# Revit family: Planet-Wattohm Mini Colonnes Logix Clippage direct
name_source: partatom
category: Installations électriques
units: mm (PartAtom-declared; Revit-internal decimal feet)

## family parameters
Basée sur le plan de construction = Non
Conserver l'orientation des annotations = Non
Cote de connecteur circulaire = Utiliser le diamètre
Couper avec des vides une fois chargée = Non
Partagée = Non
Point de calcul de pièce = Non
Toujours verticalement = Oui
Type d'élément = Normal

## types (6) — shared parameters
Column stand = Pied mobile : pied pr Colonnette Alu 1/2 cpt
Fabricant = PLANET WATTOHM
Finition = Aluminium
Matériau couvercle = Legrand - Plastique gris
Matériaux corps = Legrand - Aluminium gris
Standard = A clippage direct-ON
zero-valued in all types: Elévation par défaut

## per-type parameters (varying)
| type | 1 CPT | 2 CPT | 4 CPT | Description | H1 | HC | Largeur | Longueur | Matériau principal | Modèle | Nombre de compartiments | Séparateur |
| Colonnette 1 cpt 0,30m Alu | Oui | Non | Non | Colonne mobile 1 compartiment, 2 faces. Clippage direct. Logix 45. Corps en et couvercles en Aluminium. 2m | 300 mm | 260 mm  [stored 0.853018 ft] | 75 mm  [stored 0.246063 ft] | 82 mm  [stored 0.269029 ft] | Aluminium | PW-32315 | 1 compartiment | 35 mm |
| Colonnette 1 cpt 0,68m Alu | Oui | Non | Non | Colonnette 1 compartiment. Clippage direct. Logix 45. En Aluminium. 0,30m | 680 mm  [stored 2.23097 ft] | 640 mm  [stored 2.09974 ft] | 75 mm  [stored 0.246063 ft] | 82 mm  [stored 0.269029 ft] | Aluminium | PW-32316 | 1 compartiment | 35 mm |
| Colonnette 2 cpts 0,68m Alu | Non | Oui | Non | Colonne mobile  2 compartiments, 2 faces. Clippage direct. Logix 45. Corps en et couvercles en Aluminium. 2m | 680 mm  [stored 2.23097 ft] | 640 mm  [stored 2.09974 ft] | 75 mm  [stored 0.246063 ft] | 125 mm | Aluminium | PW-32326 | 2 compartiments | 35 mm |
| Colonnette 4 cpts 0,30m Alu | Non | Non | Oui | Colonne 4 compartiments, 2 faces. Clippage direct | 300 mm | 260 mm  [stored 0.853018 ft] | 125 mm | 125 mm | Aluminium | PW-32345 | 4 compartiments | 125 mm |
| Colonnette 4 cpts 0,68m Alu | Non | Non | Oui | Colonnette 4 compartiments. 2 faces. Clippage direct. Logix 45. En Aluminium. 0,30m | 680 mm  [stored 2.23097 ft] | 640 mm  [stored 2.09974 ft] | 125 mm | 125 mm | Aluminium | PW-32346 | 4 compartiments | 125 mm |
| roll and plug 1 cpt 0,68m Alu | Oui | Non | Non | Colonnette 1 compartiment. Clippage direct. Logix 45. En Aluminium. 0,68m | 680 mm  [stored 2.23097 ft] | 640 mm  [stored 2.09974 ft] | 75 mm  [stored 0.246063 ft] | 82 mm  [stored 0.269029 ft] | Mixte | PW-32317 | 1 compartiment | 35 mm |

note: [stored X ft] marks values corroborated as IEEE doubles in the binary element streams (Revit-internal decimal feet)
